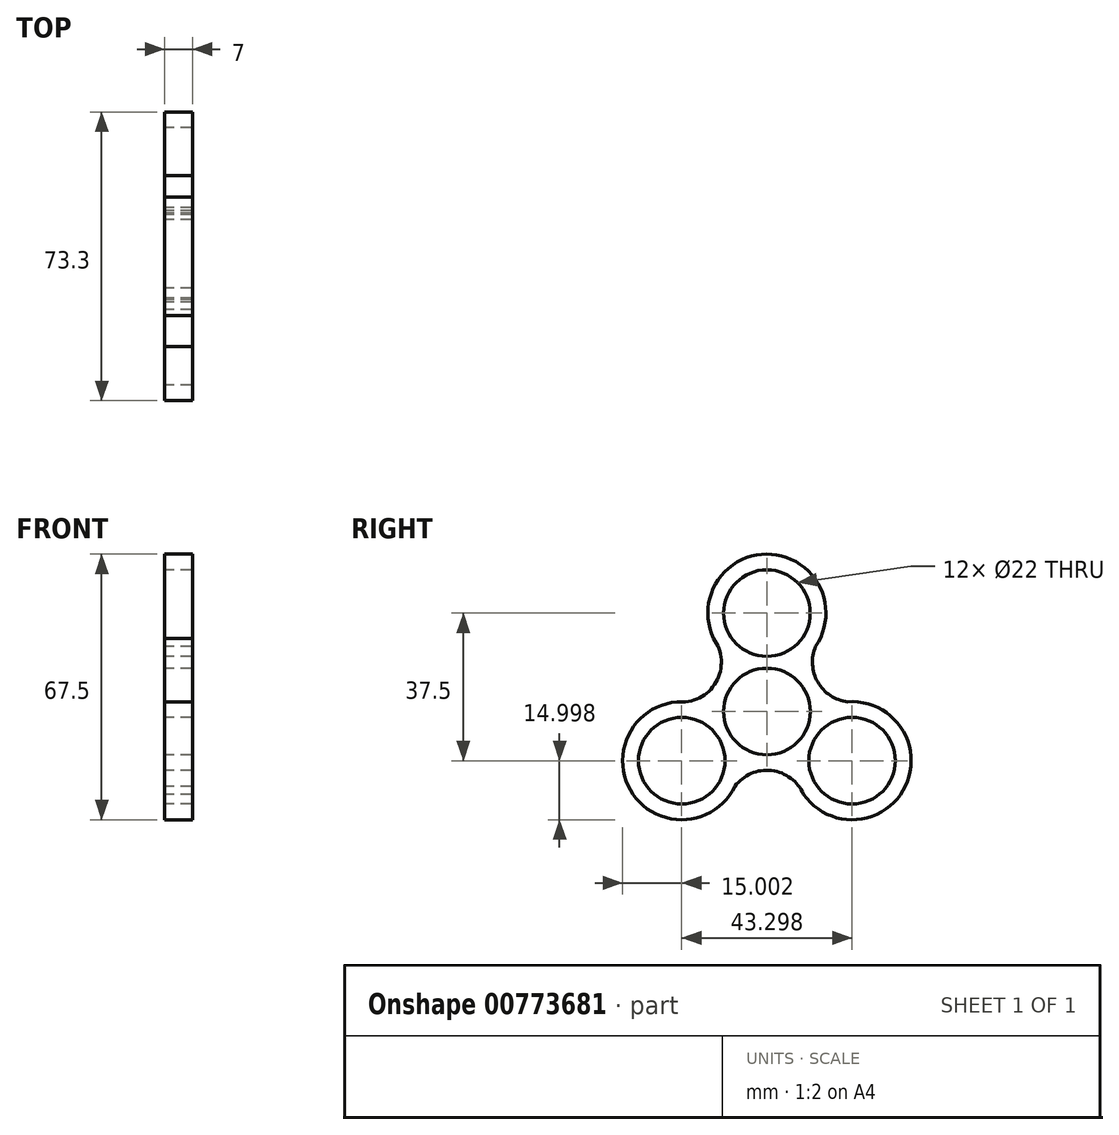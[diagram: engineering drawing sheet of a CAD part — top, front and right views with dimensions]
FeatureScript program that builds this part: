
annotation { "Feature Type Name" : "Feature", "Feature Type Description" : "" }
export const myFeature = defineFeature(function(context is Context, id is Id, definition is map)
    precondition{}
    {
        {
            var Q0;
            Q0=qCreatedBy(makeId("Right.planeOp"),FACE);
            var sketch = newSketch(context, id + "F0", { "sketchPlane" : qUnion([Q0])});
            skCircle(sketch, "E0", {"center": v(0, 25) * mm, "radius": 15 * mm});
            skCircle(sketch, "E1.1.0", {"center": v(-21.65, -12.5) * mm, "radius": 15 * mm});
            skCircle(sketch, "E1.2.0", {"center": v(21.65, -12.5) * mm, "radius": 15 * mm});
            skPoint(sketch, "E1.center", {"position": v(0, 0) * mm});
            skArc(sketch, "E2", {"start": v(-22.9, 2.45) * mm, "mid": v(-12.93, 7.47) * mm, "end": v(-13.57, 18.6) * mm});
            skArc(sketch, "E3.1.0", {"start": v(9.33, -21.05) * mm, "mid": v(0, -14.93) * mm, "end": v(-9.33, -21.05) * mm});
            skArc(sketch, "E3.2.0", {"start": v(13.57, 18.6) * mm, "mid": v(12.93, 7.47) * mm, "end": v(22.9, 2.45) * mm});
            skCircle(sketch, "E4", {"center": v(0, 0) * mm, "radius": 11 * mm});
            skCircle(sketch, "E5", {"center": v(-21.65, -12.5) * mm, "radius": 11 * mm});
            skCircle(sketch, "E6.1.0", {"center": v(21.65, -12.5) * mm, "radius": 11 * mm});
            skCircle(sketch, "E6.2.0", {"center": v(0, 25) * mm, "radius": 11 * mm});
            skSolve(sketch);
        }
        {
            var Q0;
            Q0=makeQuery(id+"F0.imprint","IMPRINT",FACE,{"disambiguationData":[TD([[makeQuery(id+"F0.imprint","IMPRINT",EDGE,{"derivedFrom":sQuery(id+"F0.wireOp",EDGE,"E5")}),-1.0]])]});
            var Q1;
            {var subQ0=sQuery(id+"F0.wireOp",EDGE,"E2");var subQ1=sQuery(id+"F0.wireOp",EDGE,"E0");var subQ2=makeQuery(id+"F0.imprint","INTERSECT",VERTEX,{"disambiguationData":[OD(1.0)],"derivedFrom":[subQ1,subQ0]});Q1=makeQuery(id+"F0.imprint","IMPRINT",FACE,{"disambiguationData":[TD([[makeQuery(id+"F0.imprint","IMPRINT",EDGE,{"disambiguationData":[TD([[subQ2,-1.0]])],"derivedFrom":subQ1}),-1.0]])]});}
            var Q2;
            Q2=makeQuery(id+"F0.imprint","IMPRINT",FACE,{"disambiguationData":[TD([[makeQuery(id+"F0.imprint","IMPRINT",EDGE,{"derivedFrom":sQuery(id+"F0.wireOp",EDGE,"E6.2.0")}),-1.0]])]});
            var Q3;
            {var subQ0=sQuery(id+"F0.wireOp",EDGE,"E3.2.0");var subQ1=sQuery(id+"F0.wireOp",EDGE,"E0");var subQ2=makeQuery(id+"F0.imprint","INTERSECT",VERTEX,{"derivedFrom":[subQ1,subQ0]});Q3=makeQuery(id+"F0.imprint","IMPRINT",FACE,{"disambiguationData":[TD([[makeQuery(id+"F0.imprint","IMPRINT",EDGE,{"disambiguationData":[TD([[subQ2,1.0]])],"derivedFrom":subQ1}),-1.0]])]});}
            var Q4;
            Q4=makeQuery(id+"F0.imprint","IMPRINT",FACE,{"disambiguationData":[TD([[makeQuery(id+"F0.imprint","IMPRINT",EDGE,{"derivedFrom":sQuery(id+"F0.wireOp",EDGE,"E6.1.0")}),-1.0]])]});
            var Q5;
            {var subQ0=sQuery(id+"F0.wireOp",EDGE,"E3.1.0");var subQ1=sQuery(id+"F0.wireOp",EDGE,"E1.1.0");var subQ2=makeQuery(id+"F0.imprint","INTERSECT",VERTEX,{"derivedFrom":[subQ1,subQ0]});Q5=makeQuery(id+"F0.imprint","IMPRINT",FACE,{"disambiguationData":[TD([[makeQuery(id+"F0.imprint","IMPRINT",EDGE,{"disambiguationData":[TD([[subQ2,-1.0]])],"derivedFrom":subQ1}),-1.0]])]});}
            extrude(context, id + "F1", {"entities" : qUnion([Q0, Q1, Q2, Q3, Q4, Q5]), "depth" : 7 * mm, "offsetDistance" : 25.4 * mm});
        }
    });
